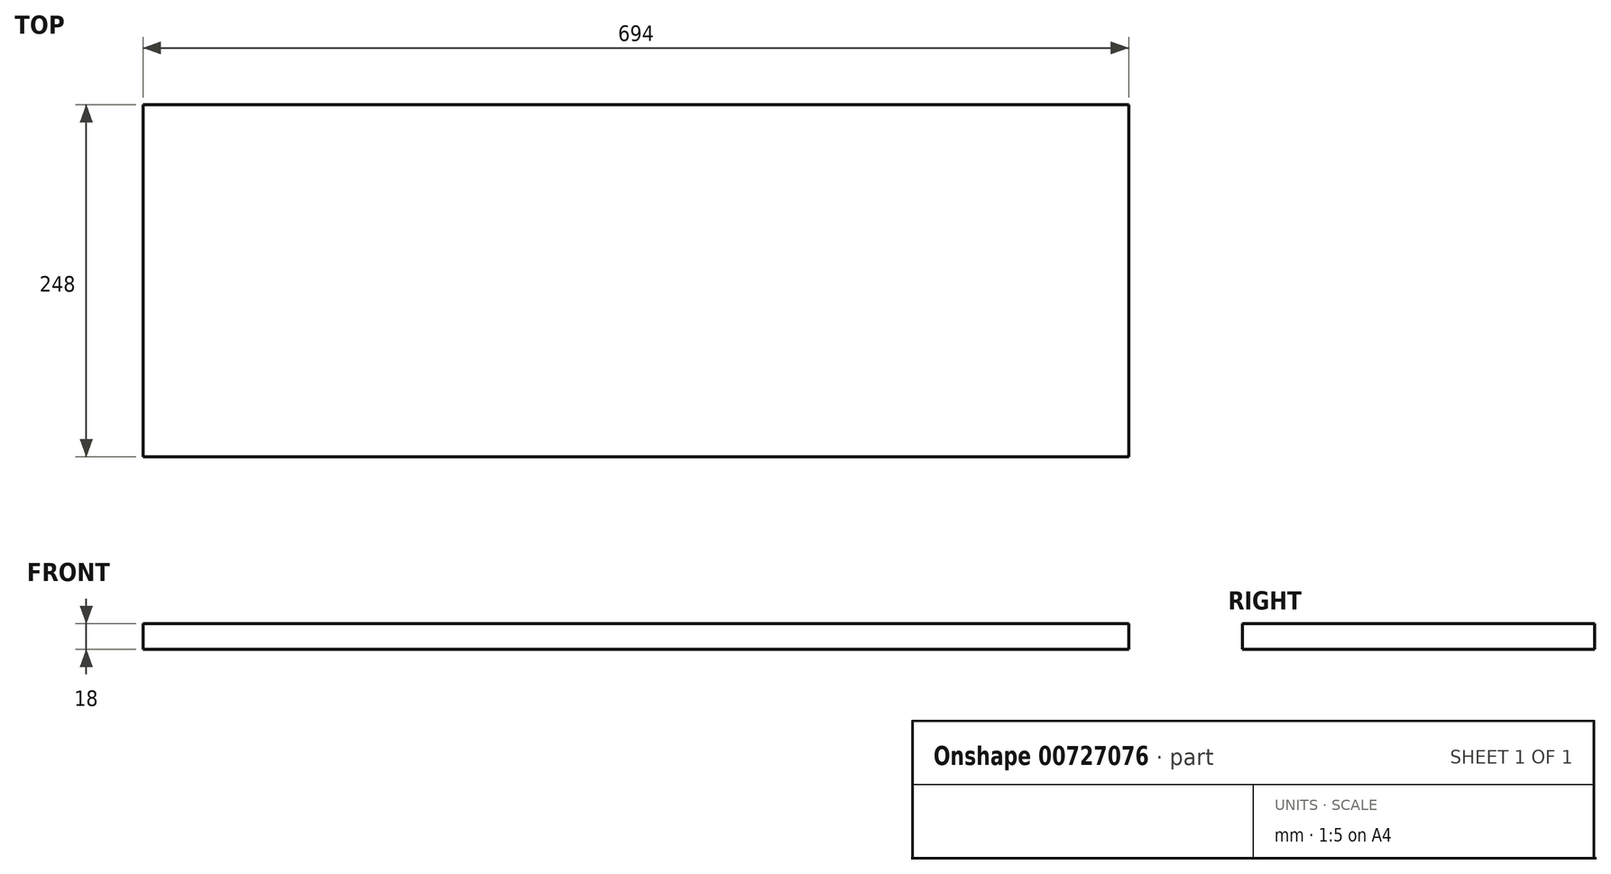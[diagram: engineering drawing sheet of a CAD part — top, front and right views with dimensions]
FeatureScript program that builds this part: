
annotation { "Feature Type Name" : "Feature", "Feature Type Description" : "" }
export const myFeature = defineFeature(function(context is Context, id is Id, definition is map)
    precondition{}
    {
        {
            var Q0;
            Q0=qCreatedBy(makeId("Top.planeOp"),FACE);
            var sketch = newSketch(context, id + "F0", { "sketchPlane" : qUnion([Q0])});
            skLineSegment(sketch, "E0.bottom", {"start": v(-314.08, -149.4) * mm, "end": v(379.92, -149.4) * mm});
            skLineSegment(sketch, "E0.top", {"start": v(-314.08, -397.4) * mm, "end": v(379.92, -397.4) * mm});
            skLineSegment(sketch, "E0.left", {"start": v(-314.08, -149.4) * mm, "end": v(-314.08, -397.4) * mm});
            skLineSegment(sketch, "E0.right", {"start": v(379.92, -149.4) * mm, "end": v(379.92, -397.4) * mm});
            skLineSegment(sketch, "E1", {"start": v(-314.08, -149.4) * mm, "end": v(379.92, -397.4) * mm, "construction": true});
            skLineSegment(sketch, "E2", {"start": v(379.92, -149.4) * mm, "end": v(-314.08, -397.4) * mm, "construction": true});
            skSolve(sketch);
        }
        {
            var Q0;
            Q0=qSketchRegion(id+"F0",true);
            extrude(context, id + "F1", {"entities" : qUnion([Q0]), "depth" : 18 * mm, "offsetDistance" : 25 * mm});
        }
    });
